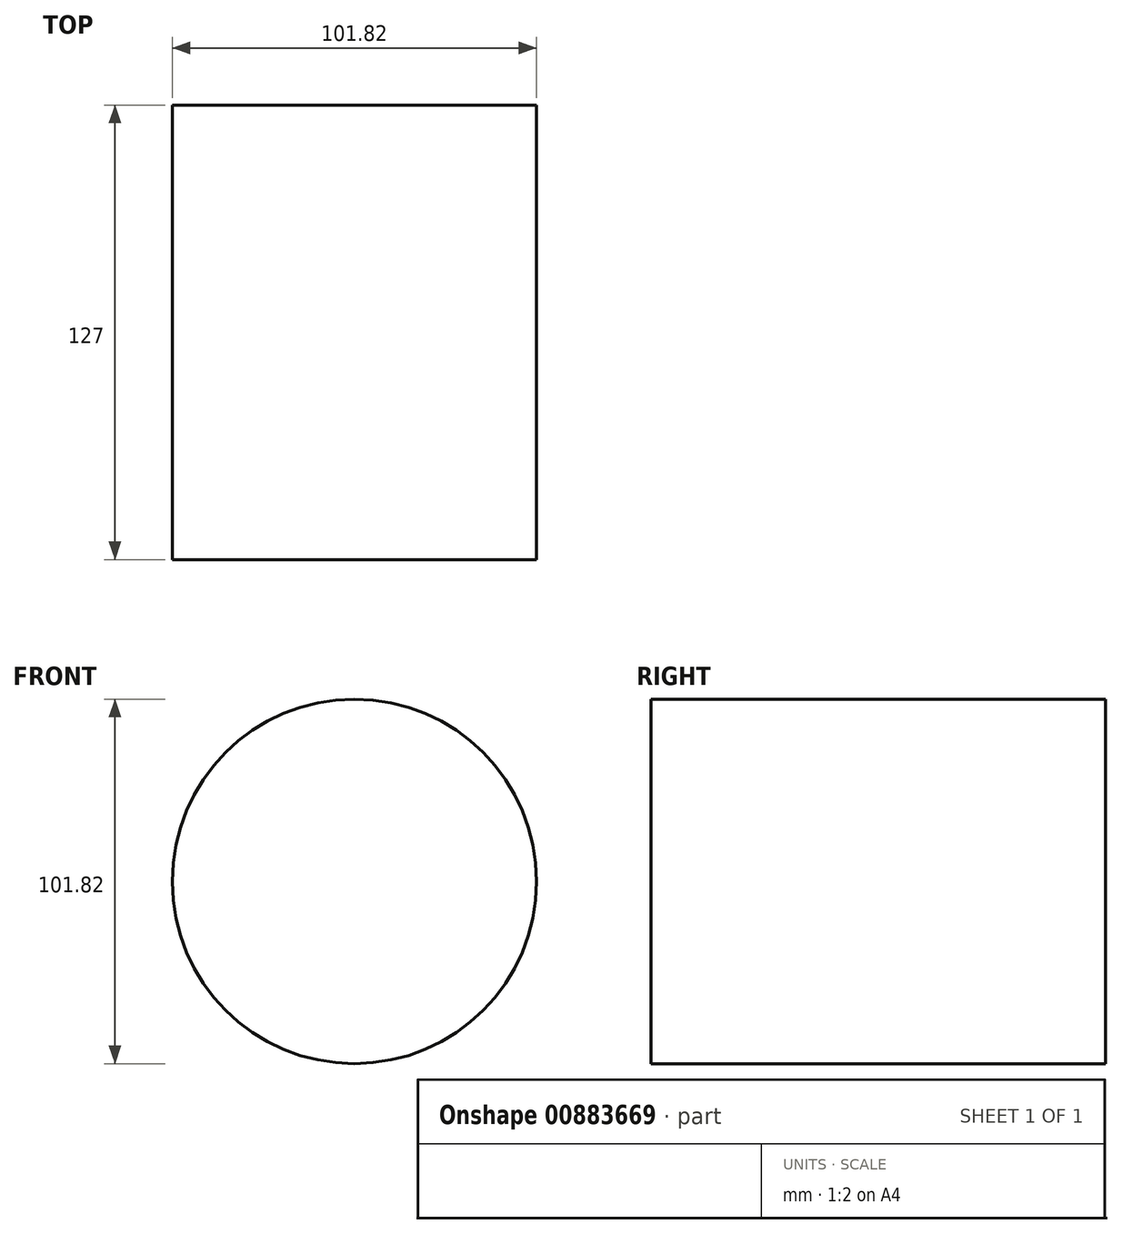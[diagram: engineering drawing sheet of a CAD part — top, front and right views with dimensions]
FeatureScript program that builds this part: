
annotation { "Feature Type Name" : "Feature", "Feature Type Description" : "" }
export const myFeature = defineFeature(function(context is Context, id is Id, definition is map)
    precondition{}
    {
        {
            var Q0;
            Q0=qCreatedBy(makeId("Front.planeOp"),FACE);
            var sketch = newSketch(context, id + "F0", { "sketchPlane" : qUnion([Q0])});
            skCircle(sketch, "E0", {"center": v(0, 0) * mm, "radius": 50.9 * mm});
            skSolve(sketch);
        }
        {
            var Q0;
            Q0=makeQuery(id+"F0.imprint","IMPRINT",FACE,{"disambiguationData":[TD([[makeQuery(id+"F0.imprint","IMPRINT",EDGE,{"derivedFrom":sQuery(id+"F0.wireOp",EDGE,"E0")}),1.0]])]});
            extrude(context, id + "F1", {"entities" : qUnion([Q0]), "depth" : 127 * mm, "offsetDistance" : 25.4 * mm});
        }
    });
